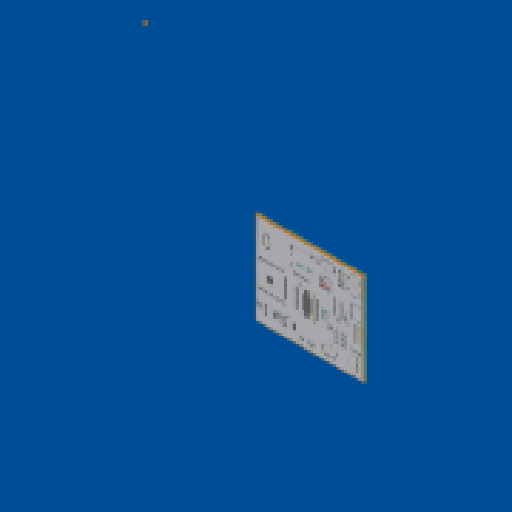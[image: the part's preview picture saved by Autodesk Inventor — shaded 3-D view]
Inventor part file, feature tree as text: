
AUTODESK INVENTOR PART (.ipt)
format: ipt  version: 2023.1 (Build 271208000, 208)  size: 252,416 bytes
history: native  units: in
note: dims shown in document units (in); Inventor stores cm internally (conversion verified against a paired STEP export)
features: sketch x1, other x1, imported_body x1
ambient origin geometry x8: Origin, YZ Plane, XZ Plane, XY Plane, X Axis, Y Axis, Z Axis, Center Point
bodies: Solid1 (feature_tree)
feature tree (3):
  sketch  "Sketch1"
  other  "Image1"
  imported_body  "Base1"
